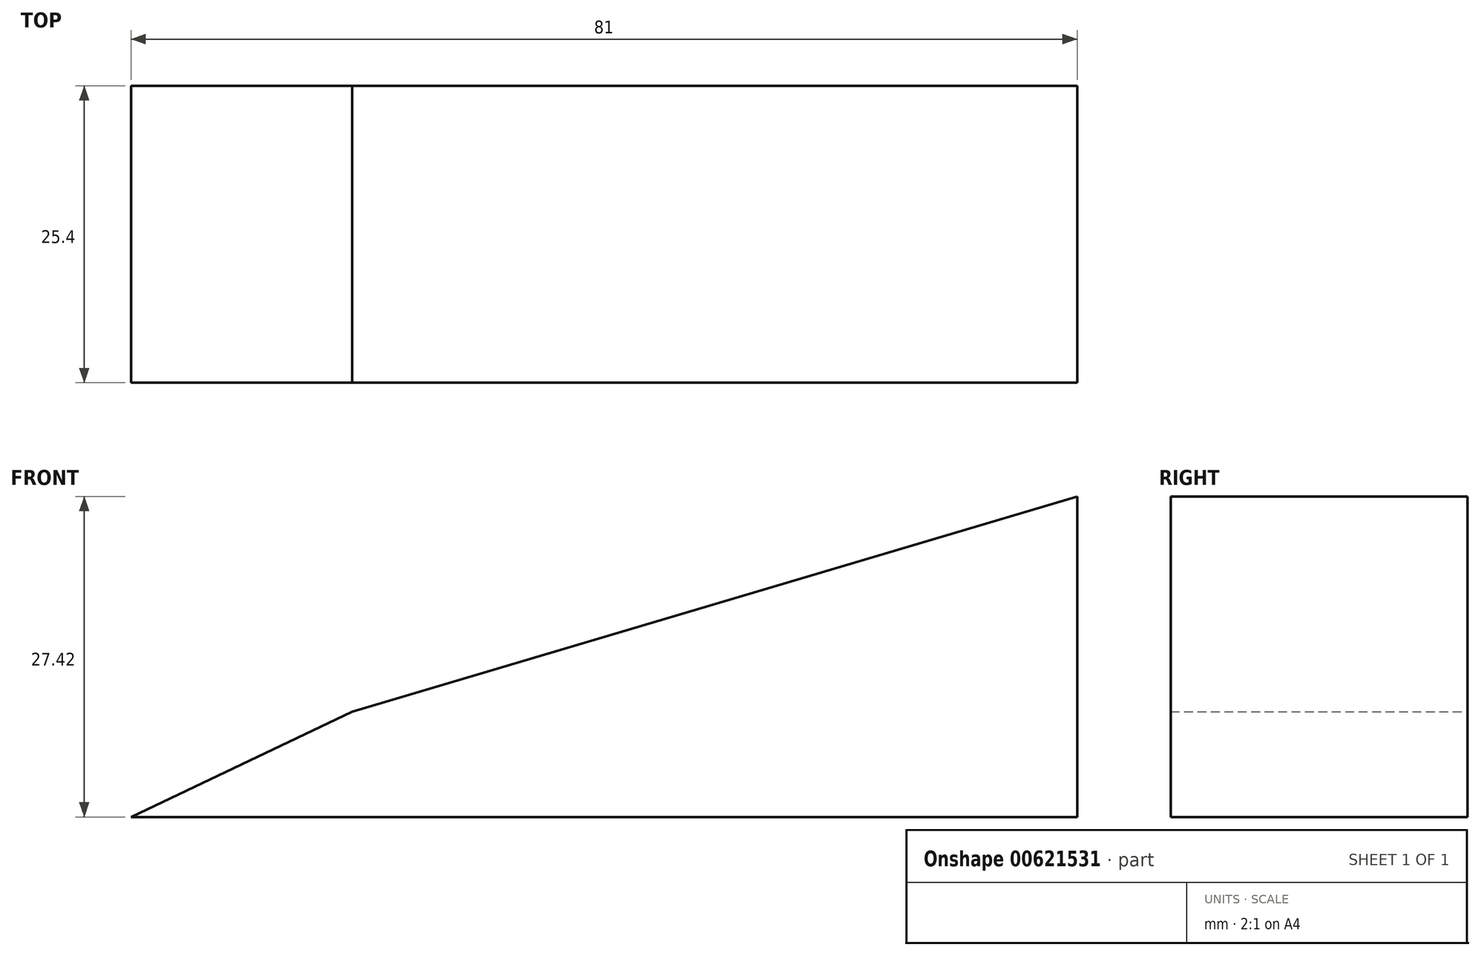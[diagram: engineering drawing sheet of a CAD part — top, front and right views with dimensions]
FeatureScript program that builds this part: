
annotation { "Feature Type Name" : "Feature", "Feature Type Description" : "" }
export const myFeature = defineFeature(function(context is Context, id is Id, definition is map)
    precondition{}
    {
        {
            var Q0;
            Q0=qCreatedBy(makeId("Front.planeOp"),FACE);
            var sketch = newSketch(context, id + "F0", { "sketchPlane" : qUnion([Q0])});
            skLineSegment(sketch, "E0", {"start": v(-22.64, -13.35) * mm, "end": v(58.36, -13.35) * mm});
            skLineSegment(sketch, "E1", {"start": v(58.36, -13.35) * mm, "end": v(58.36, 14.07) * mm});
            skLineSegment(sketch, "E2", {"start": v(58.36, 14.07) * mm, "end": v(-3.7, -4.33) * mm});
            skLineSegment(sketch, "E3", {"start": v(-3.7, -4.33) * mm, "end": v(-22.64, -13.35) * mm});
            skSolve(sketch);
        }
        {
            var Q0;
            Q0=makeQuery(id+"F0.imprint","IMPRINT",FACE,{"disambiguationData":[TD([[makeQuery(id+"F0.imprint","IMPRINT",EDGE,{"derivedFrom":sQuery(id+"F0.wireOp",EDGE,"E0")}),1.0]])]});
            extrude(context, id + "F1", {"entities" : qUnion([Q0]), "depth" : 25.4 * mm, "offsetDistance" : 25.4 * mm});
        }
    });
